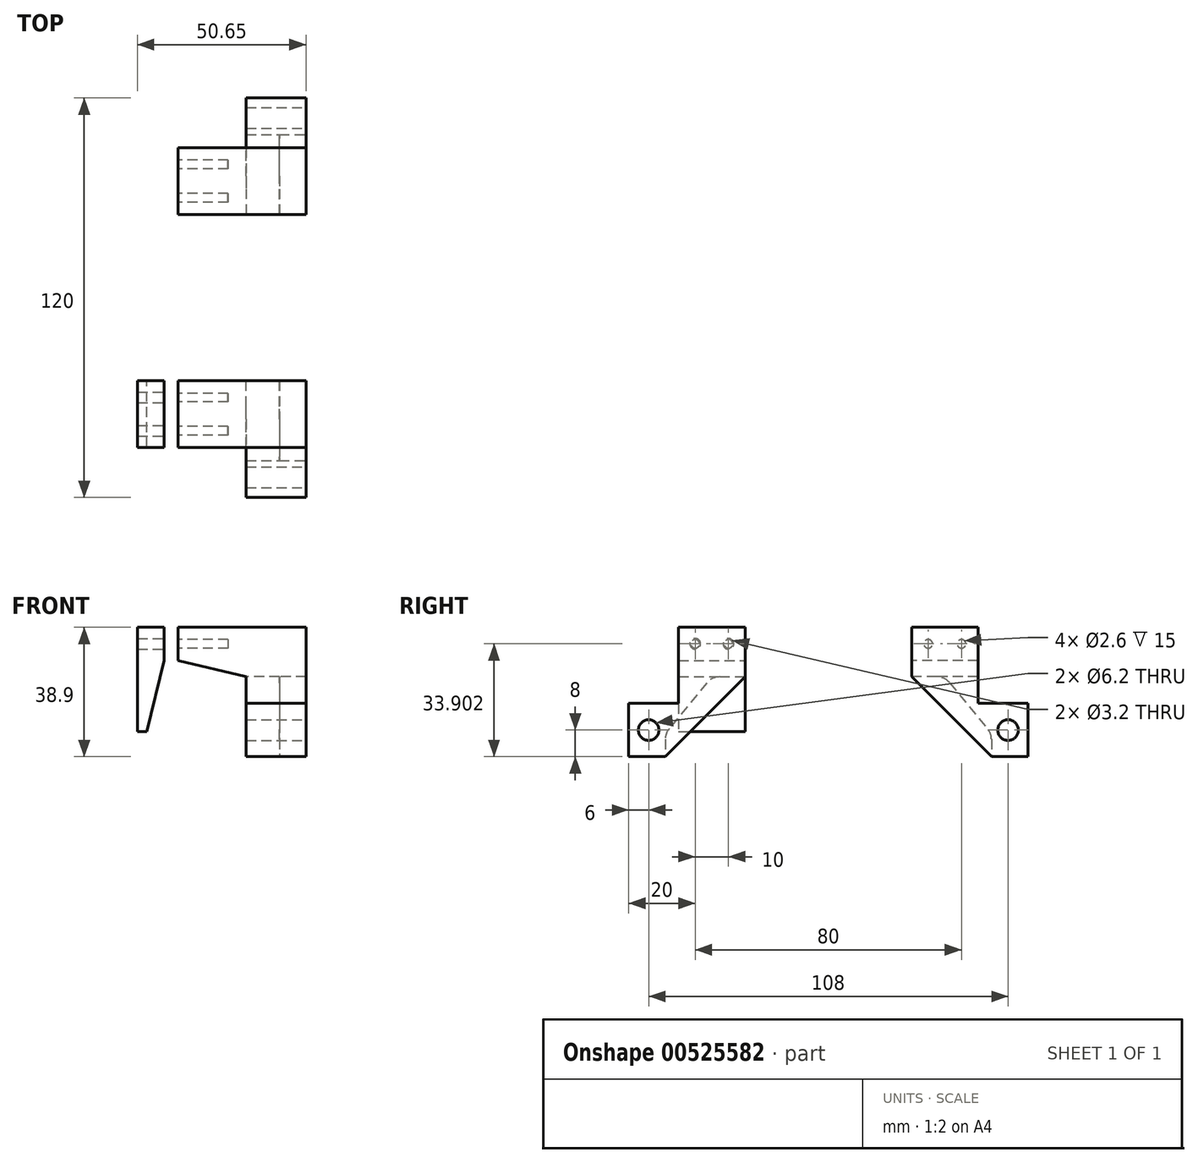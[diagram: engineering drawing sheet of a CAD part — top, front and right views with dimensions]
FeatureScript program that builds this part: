
annotation { "Feature Type Name" : "Feature", "Feature Type Description" : "" }
export const myFeature = defineFeature(function(context is Context, id is Id, definition is map)
    precondition{}
    {
        {
            var Q0;
            Q0=qCreatedBy(makeId("Front.planeOp"),FACE);
            var sketch = newSketch(context, id + "F0", { "sketchPlane" : qUnion([Q0])});
            skLineSegment(sketch, "E0", {"start": v(22.75, 23.19) * mm, "end": v(-21.3, 23.19) * mm, "construction": true});
            skLineSegment(sketch, "E1", {"start": v(-21.3, 23.19) * mm, "end": v(-21.3, -16.81) * mm, "construction": true});
            skLineSegment(sketch, "E2.bottom", {"start": v(-11.3, 13.19) * mm, "end": v(8.7, 13.19) * mm, "construction": true});
            skLineSegment(sketch, "E2.left", {"start": v(-11.3, 13.19) * mm, "end": v(-11.3, -16.81) * mm, "construction": true});
            skLineSegment(sketch, "E3", {"start": v(-21.3, -16.81) * mm, "end": v(-11.3, -16.81) * mm, "construction": true});
            skLineSegment(sketch, "E4", {"start": v(8.7, 13.19) * mm, "end": v(14.53, -11.12) * mm, "construction": true});
            skLineSegment(sketch, "E5", {"start": v(14.53, -11.12) * mm, "end": v(30.09, -7.39) * mm, "construction": true});
            skLineSegment(sketch, "E6", {"start": v(30.09, -7.39) * mm, "end": v(22.75, 23.19) * mm, "construction": true});
            skLineSegment(sketch, "E7.bottom", {"start": v(94.06, -12) * mm, "end": v(76.06, -12) * mm});
            skLineSegment(sketch, "E7.top", {"start": v(94.06, 12) * mm, "end": v(76.06, 12) * mm});
            skLineSegment(sketch, "E7.left", {"start": v(94.06, -12) * mm, "end": v(94.06, 12) * mm});
            skLineSegment(sketch, "E7.right", {"start": v(76.06, -12) * mm, "end": v(76.06, 12) * mm});
            skPoint(sketch, "E7.middle", {"position": v(85.06, 0) * mm});
            skLineSegment(sketch, "E8", {"start": v(76.06, 12) * mm, "end": v(55.64, 16.9) * mm});
            skLineSegment(sketch, "E9", {"start": v(55.64, 16.9) * mm, "end": v(55.64, 26.9) * mm});
            skLineSegment(sketch, "E10", {"start": v(55.64, 26.9) * mm, "end": v(94.06, 26.9) * mm});
            skLineSegment(sketch, "E11", {"start": v(94.06, 26.9) * mm, "end": v(94.06, 12) * mm});
            skLineSegment(sketch, "E12.bottom", {"start": v(51.4, 26.9) * mm, "end": v(43.4, 26.9) * mm});
            skLineSegment(sketch, "E12.left", {"start": v(51.4, 26.9) * mm, "end": v(51.4, 16.9) * mm});
            skLineSegment(sketch, "E12.right", {"start": v(43.4, 26.9) * mm, "end": v(43.4, -4.49) * mm});
            skLineSegment(sketch, "E13", {"start": v(51.4, 16.9) * mm, "end": v(46.27, -4.49) * mm});
            skLineSegment(sketch, "E14", {"start": v(43.4, -4.49) * mm, "end": v(46.27, -4.49) * mm});
            skSolve(sketch);
        }
        {
            var Q0;
            Q0 = qSketchRegion(id + "F0", true);
            extrude(context, id + "F1", {"entities" : qUnion([Q0]), "depth" : 20 * mm, "offsetDistance" : 25 * mm});
        }
        {
            var Q0;
            Q0=makeQuery(id+"F1.opExtrude","SWEPT_FACE",FACE,{"disambiguationData":[OSD([sQuery(id+"F0.wireOp",EDGE,"E9")])]});
            var sketch = newSketch(context, id + "F2", { "sketchPlane" : qUnion([Q0])});
            skCircle(sketch, "E15", {"center": v(15, 21.9) * mm, "radius": 1.3 * mm});
            skCircle(sketch, "E16", {"center": v(5, 21.9) * mm, "radius": 1.3 * mm});
            skSolve(sketch);
        }
        {
            var Q0;
            Q0 = qSketchRegion(id + "F2", true);
            extrude(context, id + "F3", {"entities" : qUnion([Q0]), "operationType" : NewBodyOperationType.REMOVE, "oppositeDirection" : true, "depth" : 15 * mm, "offsetDistance" : 25 * mm});
        }
        {
            var Q0;
            Q0=makeQuery(id+"F1.opExtrude","SWEPT_FACE",FACE,{"disambiguationData":[OSD([sQuery(id+"F0.wireOp",EDGE,"E12.left")])]});
            var sketch = newSketch(context, id + "F4", { "sketchPlane" : qUnion([Q0])});
            skCircle(sketch, "E17", {"center": v(-15, 21.9) * mm, "radius": 1.6 * mm});
            skPoint(sketch, "E17.centerSnap0", {"position": v(-20, 21.9) * mm});
            skCircle(sketch, "E18", {"center": v(-5, 21.9) * mm, "radius": 1.6 * mm});
            skSolve(sketch);
        }
        {
            var Q0;
            Q0 = qSketchRegion(id + "F4", true);
            extrude(context, id + "F5", {"entities" : qUnion([Q0]), "operationType" : NewBodyOperationType.REMOVE, "oppositeDirection" : true, "depth" : 10 * mm, "offsetDistance" : 25 * mm});
        }
        {
            var Q0;
            Q0=makeQuery(id+"F1.opExtrude","CAP_FACE",FACE,{"disambiguationData":[OSD([sQuery(id+"F0.wireOp",EDGE,"E7.bottom"),sQuery(id+"F0.wireOp",EDGE,"E7.left"),sQuery(id+"F0.wireOp",EDGE,"E7.right"),sQuery(id+"F0.wireOp",EDGE,"E8"),sQuery(id+"F0.wireOp",EDGE,"E9"),sQuery(id+"F0.wireOp",EDGE,"E10"),sQuery(id+"F0.wireOp",EDGE,"E11")])],"isStart":false});
            var sketch = newSketch(context, id + "F6", { "sketchPlane" : qUnion([Q0])});
            skLineSegment(sketch, "E19.bottom", {"start": v(76.06, -12) * mm, "end": v(94.06, -12) * mm});
            skLineSegment(sketch, "E19.top", {"start": v(76.06, 4) * mm, "end": v(94.06, 4) * mm});
            skLineSegment(sketch, "E19.left", {"start": v(76.06, -12) * mm, "end": v(76.06, 4) * mm});
            skLineSegment(sketch, "E19.right", {"start": v(94.06, -12) * mm, "end": v(94.06, 4) * mm});
            skSolve(sketch);
        }
        {
            var Q0;
            Q0 = qSketchRegion(id + "F6", true);
            extrude(context, id + "F7", {"entities" : qUnion([Q0]), "operationType" : NewBodyOperationType.ADD, "depth" : 15 * mm, "offsetDistance" : 25 * mm});
        }
        {
            var Q0;
            Q0=makeQuery(id+"F7.boolean.opBoolean","MERGE",FACE,{"derivedFrom":[makeQuery(id+"F1.opExtrude","SWEPT_FACE",FACE,{"disambiguationData":[OSD([sQuery(id+"F0.wireOp",EDGE,"E7.left"),sQuery(id+"F0.wireOp",EDGE,"E11")])]}),makeQuery(id+"F7.opExtrude","SWEPT_FACE",FACE,{"disambiguationData":[OSD([sQuery(id+"F6.wireOp",EDGE,"E19.right")])]})]});
            var sketch = newSketch(context, id + "F8", { "sketchPlane" : qUnion([Q0])});
            skCircle(sketch, "E20", {"center": v(-29, -4) * mm, "radius": 3.1 * mm});
            skSolve(sketch);
        }
        {
            var Q0;
            Q0 = qSketchRegion(id + "F8", true);
            extrude(context, id + "F9", {"entities" : qUnion([Q0]), "operationType" : NewBodyOperationType.REMOVE, "endBound" : BoundingType.THROUGH_ALL, "oppositeDirection" : true, "depth" : 25 * mm, "offsetDistance" : 25 * mm});
        }
        {
            var Q0;
            Q0=makeQuery(id+"F1.opExtrude","CAP_EDGE",EDGE,{"disambiguationData":[OSD([sQuery(id+"F0.wireOp",EDGE,"E7.bottom")])],"isStart":true});
            chamfer(context, id + "F10", {"entities" : qUnion([Q0]), "width" : 24 * mm, "tangentPropagation" : true});
        }
        {
            var Q0;
            Q0=makeQuery(id+"F7.boolean.opBoolean","MERGE",FACE,{"derivedFrom":[makeQuery(id+"F1.opExtrude","SWEPT_FACE",FACE,{"disambiguationData":[OSD([sQuery(id+"F0.wireOp",EDGE,"E7.right")])]}),makeQuery(id+"F7.opExtrude","SWEPT_FACE",FACE,{"disambiguationData":[OSD([sQuery(id+"F6.wireOp",EDGE,"E19.left")])]})]});
            var sketch = newSketch(context, id + "F11", { "sketchPlane" : qUnion([Q0])});
            skLineSegment(sketch, "E21", {"start": v(0, 12) * mm, "end": v(10, 12) * mm});
            skLineSegment(sketch, "E22", {"start": v(10, 12) * mm, "end": v(24, -5) * mm});
            skLineSegment(sketch, "E23", {"start": v(24, -5) * mm, "end": v(24, -12) * mm});
            skLineSegment(sketch, "E24", {"start": v(24, -12) * mm, "end": v(0, 12) * mm});
            skSolve(sketch);
        }
        {
            var Q0;
            Q0 = qSketchRegion(id + "F11", true);
            extrude(context, id + "F12", {"entities" : qUnion([Q0]), "operationType" : NewBodyOperationType.REMOVE, "oppositeDirection" : true, "depth" : 10 * mm, "offsetDistance" : 25 * mm});
        }
        {
            var Q0;
            Q0=makeQuery(id+"F7.opExtrude","CAP_EDGE",EDGE,{"disambiguationData":[OSD([sQuery(id+"F6.wireOp",EDGE,"E19.top")])],"isStart":true});
            var Q1;
            Q1=makeQuery(id+"F12.boolean.opBoolean","COPY",EDGE,{"derivedFrom":makeQuery(id+"F12.opExtrude","SWEPT_EDGE",EDGE,{"disambiguationData":[OSD([sQuery(id+"F11.wireOp",EDGE,"E22"),sQuery(id+"F11.wireOp",EDGE,"E23")])]})});
            var Q2;
            Q2=makeQuery(id+"F12.boolean.opBoolean","COPY",EDGE,{"derivedFrom":makeQuery(id+"F12.opExtrude","SWEPT_EDGE",EDGE,{"disambiguationData":[OSD([sQuery(id+"F0.wireOp",EDGE,"E7.top"),sQuery(id+"F0.wireOp",EDGE,"E7.right"),sQuery(id+"F0.wireOp",EDGE,"E8"),sQuery(id+"F11.wireOp",EDGE,"E21"),sQuery(id+"F11.wireOp",EDGE,"E22")])]})});
            fillet(context, id + "F13", {"entities" : qUnion([Q0, Q1, Q2]), "radius" : 5 * mm, "tangentPropagation" : true, "allowEdgeOverflow" : false});
        }
        {
            var Q0;
            Q0=makeQuery(id+"F1.opExtrude","CAP_FACE",FACE,{"disambiguationData":[OSD([sQuery(id+"F0.wireOp",EDGE,"E7.bottom"),sQuery(id+"F0.wireOp",EDGE,"E7.left"),sQuery(id+"F0.wireOp",EDGE,"E7.right"),sQuery(id+"F0.wireOp",EDGE,"E8"),sQuery(id+"F0.wireOp",EDGE,"E9"),sQuery(id+"F0.wireOp",EDGE,"E10"),sQuery(id+"F0.wireOp",EDGE,"E11")])],"isStart":true});
            cPlane(context, id + "F14", {"entities" : qUnion([Q0]), "cplaneType" : CPlaneType.OFFSET, "offset" : 25 * mm, "width" : 150 * mm, "height" : 150 * mm});
        }
        {
            var Q0;
            Q0=makeQuery(id+"F1.opExtrude","SWEPT_BODY",BODY,{"disambiguationData":[OSD([sQuery(id+"F0.wireOp",EDGE,"E7.bottom"),sQuery(id+"F0.wireOp",EDGE,"E7.left"),sQuery(id+"F0.wireOp",EDGE,"E7.right"),sQuery(id+"F0.wireOp",EDGE,"E8"),sQuery(id+"F0.wireOp",EDGE,"E9"),sQuery(id+"F0.wireOp",EDGE,"E10"),sQuery(id+"F0.wireOp",EDGE,"E11")])]});
            var Q1;
            Q1=qCreatedBy(id+"F14.planeOp",FACE);
            mirror(context, id + "F15", {"entities" : qUnion([Q0]), "mirrorPlane" : qUnion([Q1])});
        }
    });
